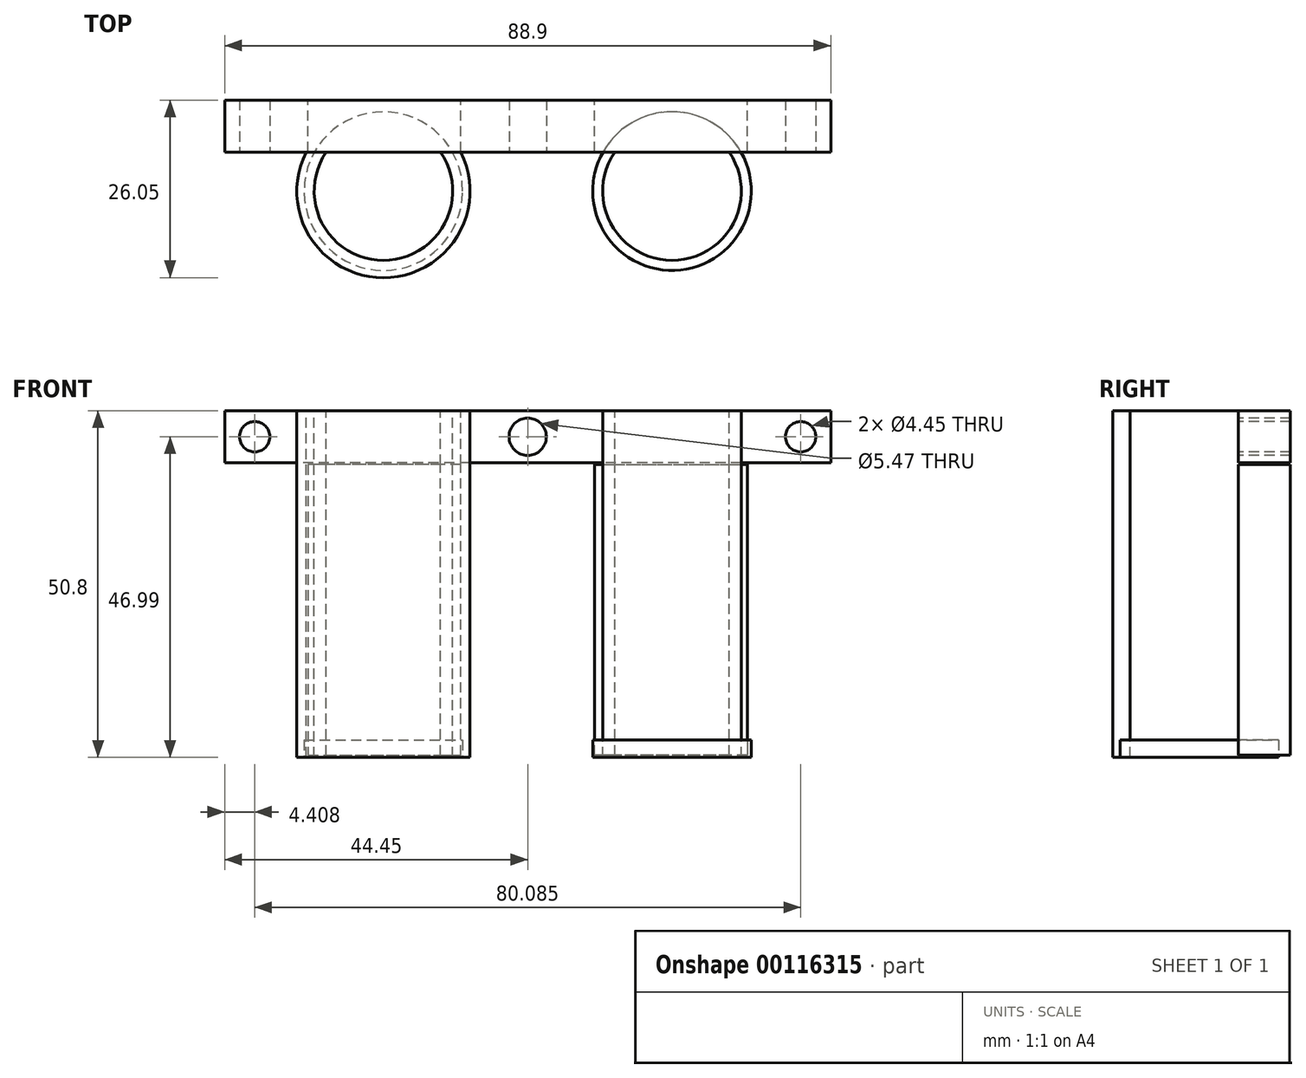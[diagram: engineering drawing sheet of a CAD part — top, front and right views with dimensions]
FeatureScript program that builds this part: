
annotation { "Feature Type Name" : "Feature", "Feature Type Description" : "" }
export const myFeature = defineFeature(function(context is Context, id is Id, definition is map)
    precondition{}
    {
        {
            var Q0;
            Q0=qCreatedBy(makeId("Front.planeOp"),FACE);
            var sketch = newSketch(context, id + "F0", { "sketchPlane" : qUnion([Q0])});
            skLineSegment(sketch, "E0.bottom", {"start": v(44.45, -3.81) * mm, "end": v(-44.45, -3.81) * mm});
            skLineSegment(sketch, "E0.top", {"start": v(44.45, 3.81) * mm, "end": v(-44.45, 3.8) * mm});
            skLineSegment(sketch, "E0.left", {"start": v(44.45, -3.81) * mm, "end": v(44.45, 3.81) * mm});
            skLineSegment(sketch, "E0.right", {"start": v(-44.45, -3.81) * mm, "end": v(-44.45, 3.8) * mm});
            skPoint(sketch, "E0.middle", {"position": v(0, 0) * mm});
            skSolve(sketch);
        }
        {
            var Q0;
            Q0=makeQuery(id+"F0.imprint","IMPRINT",FACE,{"disambiguationData":[TD([[makeQuery(id+"F0.imprint","IMPRINT",EDGE,{"derivedFrom":sQuery(id+"F0.wireOp",EDGE,"E0.bottom")}),-1.0]])]});
            extrude(context, id + "F1", {"entities" : qUnion([Q0]), "depth" : 7.62 * mm});
        }
        {
            var Q0;
            Q0=makeQuery(id+"F1.opExtrude","SWEPT_FACE",FACE,{"disambiguationData":[OSD([sQuery(id+"F0.wireOp",EDGE,"E0.top")])]});
            var sketch = newSketch(context, id + "F2", { "sketchPlane" : qUnion([Q0])});
            skArc(sketch, "E1", {"start": v(-32.5, -7.62) * mm, "mid": v(-21.16, -26.05) * mm, "end": v(-9.83, -7.62) * mm});
            skArc(sketch, "E2", {"start": v(-29.55, -7.62) * mm, "mid": v(-21.16, -23.51) * mm, "end": v(-12.77, -7.62) * mm});
            skArc(sketch, "E3.MirrorCS", {"start": v(29.55, -7.62) * mm, "mid": v(21.16, -23.51) * mm, "end": v(12.77, -7.62) * mm});
            skArc(sketch, "E4.MirrorCS", {"start": v(32.5, -7.62) * mm, "mid": v(21.16, -26.05) * mm, "end": v(9.83, -7.62) * mm});
            skSolve(sketch);
        }
        {
            var Q0;
            Q0 = qSketchRegion(id + "F2", true);
            var Q1;
            {var subQ0=sQuery(id+"F2.wireOp",EDGE,"E1");Q1=makeQuery(id+"F2.imprint","IMPRINT",FACE,{"disambiguationData":[TD([[makeQuery(id+"F2.imprint","IMPRINT",EDGE,{"derivedFrom":subQ0}),1.0]])]});}
            var Q2;
            {var subQ0=sQuery(id+"F2.wireOp",EDGE,"E3.MirrorCS");Q2=makeQuery(id+"F2.imprint","IMPRINT",FACE,{"disambiguationData":[TD([[makeQuery(id+"F2.imprint","IMPRINT",EDGE,{"derivedFrom":subQ0}),1.0]])]});}
            extrude(context, id + "F3", {"entities" : qUnion([Q0, Q1, Q2]), "oppositeDirection" : true, "depth" : 50.8 * mm});
        }
        {
            var Q0;
            Q0=qCreatedBy(makeId("Front.planeOp"),FACE);
            var sketch = newSketch(context, id + "F4", { "sketchPlane" : qUnion([Q0])});
            skLineSegment(sketch, "E5", {"start": v(-32.22, -46.7) * mm, "end": v(-9.83, -46.7) * mm});
            skLineSegment(sketch, "E6", {"start": v(-9.83, -46.7) * mm, "end": v(-9.83, -4.1) * mm});
            skLineSegment(sketch, "E7", {"start": v(-9.83, -4.1) * mm, "end": v(-32.22, -4.1) * mm});
            skLineSegment(sketch, "E8", {"start": v(-32.22, -4.1) * mm, "end": v(-32.22, -46.7) * mm});
            skLineSegment(sketch, "E9", {"start": v(0, 0) * mm, "end": v(0, -56.03) * mm, "construction": true});
            skLineSegment(sketch, "E10.MirrorCS", {"start": v(32.22, -46.7) * mm, "end": v(9.83, -46.7) * mm});
            skLineSegment(sketch, "E11.MirrorCS", {"start": v(9.83, -46.7) * mm, "end": v(9.83, -4.1) * mm});
            skLineSegment(sketch, "E12.MirrorCS", {"start": v(32.22, -4.1) * mm, "end": v(32.22, -46.7) * mm});
            skLineSegment(sketch, "E13.MirrorCS", {"start": v(9.83, -4.1) * mm, "end": v(32.22, -4.1) * mm});
            skSolve(sketch);
        }
        {
            var Q0;
            Q0 = qSketchRegion(id + "F4", true);
            extrude(context, id + "F5", {"entities" : qUnion([Q0]), "operationType" : NewBodyOperationType.ADD, "depth" : 7.62 * mm});
        }
        {
            var Q0;
            Q0=makeQuery(id+"F3.opExtrude","CAP_FACE",FACE,{"disambiguationData":[OSD([sQuery(id+"F0.wireOp",EDGE,"E0.top"),sQuery(id+"F2.wireOp",EDGE,"E3.MirrorCS"),sQuery(id+"F2.wireOp",EDGE,"E4.MirrorCS")])],"isStart":false});
            var sketch = newSketch(context, id + "F6", { "sketchPlane" : qUnion([Q0])});
            skCircle(sketch, "E14", {"center": v(21.16, 13.35) * mm, "radius": 11.63 * mm});
            skCircle(sketch, "E15.MirrorC", {"center": v(-21.16, 13.35) * mm, "radius": 11.63 * mm});
            skSolve(sketch);
        }
        {
            var Q0;
            Q0 = qSketchRegion(id + "F6", true);
            extrude(context, id + "F7", {"entities" : qUnion([Q0]), "oppositeDirection" : true, "depth" : 2.54 * mm});
        }
        {
            var Q0;
            Q0=makeQuery(id+"F1.opExtrude","CAP_FACE",FACE,{"disambiguationData":[OSD([sQuery(id+"F0.wireOp",EDGE,"E0.bottom"),sQuery(id+"F0.wireOp",EDGE,"E0.top"),sQuery(id+"F0.wireOp",EDGE,"E0.left"),sQuery(id+"F0.wireOp",EDGE,"E0.right")])],"isStart":false});
            var sketch = newSketch(context, id + "F8", { "sketchPlane" : qUnion([Q0])});
            skPoint(sketch, "E16.centerSnap0", {"position": v(-44.45, 0) * mm});
            skCircle(sketch, "E17", {"center": v(-40.04, 0) * mm, "radius": 2.22 * mm});
            skCircle(sketch, "E18.MirrorC", {"center": v(40.04, 0) * mm, "radius": 2.22 * mm});
            skSolve(sketch);
        }
        {
            var Q0;
            Q0 = qSketchRegion(id + "F8", true);
            extrude(context, id + "F9", {"entities" : qUnion([Q0]), "operationType" : NewBodyOperationType.REMOVE, "endBound" : BoundingType.THROUGH_ALL, "oppositeDirection" : true, "depth" : 25.4 * mm});
        }
        {
            var Q0;
            Q0=makeQuery(id+"F1.opExtrude","CAP_FACE",FACE,{"disambiguationData":[OSD([sQuery(id+"F0.wireOp",EDGE,"E0.bottom"),sQuery(id+"F0.wireOp",EDGE,"E0.top"),sQuery(id+"F0.wireOp",EDGE,"E0.left"),sQuery(id+"F0.wireOp",EDGE,"E0.right")])],"isStart":false});
            var sketch = newSketch(context, id + "F10", { "sketchPlane" : qUnion([Q0])});
            skCircle(sketch, "E19", {"center": v(0, 0) * mm, "radius": 2.73 * mm});
            skSolve(sketch);
        }
        {
            var Q0;
            Q0 = qSketchRegion(id + "F10", true);
            extrude(context, id + "F11", {"entities" : qUnion([Q0]), "operationType" : NewBodyOperationType.REMOVE, "oppositeDirection" : true, "depth" : 25.4 * mm});
        }
    });
